# Revit family: Faucet-Single-Grohe-Atrio-24350
name_source: partatom
category: Plumbing Fixtures
units: mm (PartAtom-declared; Revit-internal decimal feet)

## family parameters
Always vertical = No
Cut with Voids When Loaded = No
OmniClass Number = 23.45.55.14
OmniClass Title = Single Faucets
Part Type = Normal
Room Calculation Point = No
Round Connector Dimension = Use Diameter
Shared = Yes
Work Plane-Based = Yes

## types (4) — shared parameters
ADA Compliant = Yes
Assembly Code = D2020300
CW Connection = No
CWFU = 3
Default Elevation = 0"
Description = Atrio Single Hole Single Handle L-Size Bathroom Faucet 1.2gpm
Flow Rate = 1.2 gpm
HW Connection = No
HWFU = 3
Height = 11 7/8"
Installation Type = Deck-Mounted
Manufacturer = Grohe
Spout Height = 7 15/16"
Spout Reach = 6 9/16"
Tempered Water Connection = Yes
Tempered Water Connection Diameter = 3/8"
Tempered Water Connection Radius = 3/16"
URL = https://www.grohe.us
Vent Connection = No
WFU = 4
Waste Connection = No
Width = 1 5/16"

## per-type parameters (varying)
| type | Finish | Material | Product Documentation Link | Product Page URL |
| 24350000 | Metal-Grohe-000-StarLight Chrome | Metal-Grohe-000-StarLight Chrome | https://lixil.cdn.celum.cloud | https://www.grohe.us |
| 243502430 | Metal-Grohe-2430-Matte Black | Metal-Grohe-2430-Matte Black | https://lixil.cdn.celum.cloud | https://www.grohe.us |
| 24350EN0 | Metal-Grohe-EN0-Brushed Nickel Infinity Finish | Metal-Grohe-EN0-Brushed Nickel Infinity Finish |  |  |
| 24350GN0 | Metal-Grohe-GN0-Brushed Cool Sunrise | Metal-Grohe-GN0-Brushed Cool Sunrise | https://lixil.cdn.celum.cloud | https://www.grohe.us |

note: column(s) folded — value = type name in every type: Model

## geometry (parser evidence)
native form markers: Sweep x2
no freeform markers — native parametric forms only
